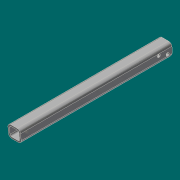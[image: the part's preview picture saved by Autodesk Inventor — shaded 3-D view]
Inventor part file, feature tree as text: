
AUTODESK INVENTOR PART (.ipt)
format: ipt  version: 2017 (Build 210142000, 142)  size: 178,688 bytes
history: native  units: mm (DEFAULTED — no unit token found)
features: sketch x5, other x3, hole x2, extrude x1, plane x1
ambient origin geometry x8: Origin, YZ Plane, XZ Plane, XY Plane, X Axis, Y Axis, Z Axis, Center Point
bodies: Solid1 (feature_tree), Body (feature_tree)
feature tree (12):
  other  "Driven Length"
  other  "Start plane"
  other  "End plane"
  extrude  "Extrusion2"  TaperAngle=0.0deg  [1 undecoded]
  hole  "Hole1"  [1 undecoded]
  hole  "Hole2"  [1 undecoded]
  sketch  "Sketch"  dims[d15=25.4mm d16=25.4mm d17=12.7mm d18=90.0deg d19=609.6mm d20=0.872665mm d21=25.4mm d22=0.0mm d23=19.05mm d24=25.4mm d25=25.4mm d26=12.7mm d27=19.05mm d28=9.525mm d29=6.35mm d30=14.3117mm d31=25.4mm d32=20.594885mm d33=53.975mm d34=6.35mm d35=12.7mm d36=19.05mm d37=9.525mm d38=6.35mm d39=14.3117mm d40=25.4mm d41=20.594885mm]
  sketch  "Sketch3"  dims[d3=609.6mm d4=0.0mm]
  plane  "Work Plane3"
  sketch  "Sketch4"  dims[d10=50.8mm d11=50.8mm]
  sketch  "Sketch5"  dims[d12=6.35mm d13=-0.0mm]
  sketch  "Sketch6"  dims[d14=609.6mm]
note: 3 required parameter values undecoded (feature->parameter linkage not recoverable at this tier; creation-order binding heuristic only, values carry confidence <= 0.55)
